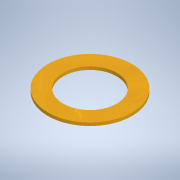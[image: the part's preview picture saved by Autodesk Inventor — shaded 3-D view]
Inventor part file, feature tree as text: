
AUTODESK INVENTOR PART (.ipt)
format: ipt  version: 2021.3 (Build 253353000, 353)  size: 104,960 bytes
history: native  units: mm
features: extrude x1, sketch x1
ambient origin geometry x8: Origin, YZ Plane, XZ Plane, XY Plane, X Axis, Y Axis, Z Axis, Center Point
bodies: Solid1 (feature_tree)
feature tree (2):
  extrude  "Extrusion1"  Depth=1.0mm
  sketch  "Sketch1"  dims[d0=17.5mm d1=5.0mm d2=1.0mm d3=0.0mm d4=0.5mm d5=0.872665mm]
